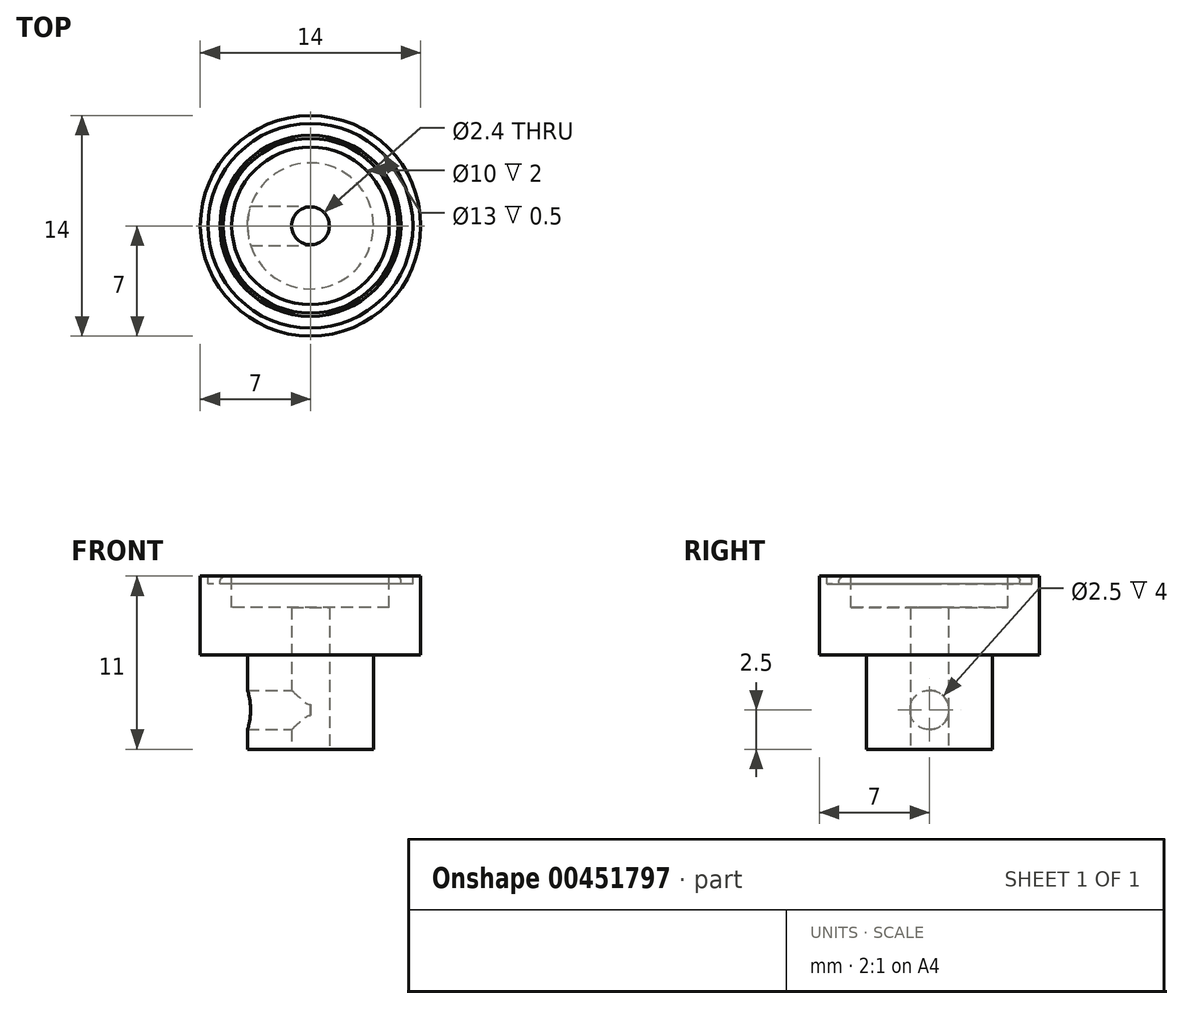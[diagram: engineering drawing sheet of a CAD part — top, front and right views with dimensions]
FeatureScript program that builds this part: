
annotation { "Feature Type Name" : "Feature", "Feature Type Description" : "" }
export const myFeature = defineFeature(function(context is Context, id is Id, definition is map)
    precondition{}
    {
        {
            var Q0;
            Q0=qCreatedBy(makeId("Top.planeOp"),FACE);
            var sketch = newSketch(context, id + "F0", { "sketchPlane" : qUnion([Q0])});
            skCircle(sketch, "E0", {"center": v(0, 0) * mm, "radius": 7 * mm});
            skSolve(sketch);
        }
        {
            var Q0;
            Q0 = qSketchRegion(id + "F0", true);
            extrude(context, id + "F1", {"entities" : qUnion([Q0]), "depth" : 5 * mm});
        }
        {
            var Q0;
            Q0=makeQuery(id+"F1.opExtrude","CAP_FACE",FACE,{"disambiguationData":[OSD([sQuery(id+"F0.wireOp",EDGE,"E0")])],"isStart":true});
            var sketch = newSketch(context, id + "F2", { "sketchPlane" : qUnion([Q0])});
            skCircle(sketch, "E1", {"center": v(0, 0) * mm, "radius": 4 * mm});
            skSolve(sketch);
        }
        {
            var Q0;
            Q0 = qSketchRegion(id + "F2", true);
            extrude(context, id + "F3", {"entities" : qUnion([Q0]), "operationType" : NewBodyOperationType.ADD, "depth" : 6 * mm});
        }
        {
            var Q0;
            Q0=makeQuery(id+"F3.opExtrude","CAP_FACE",FACE,{"disambiguationData":[OSD([sQuery(id+"F2.wireOp",EDGE,"E1")])],"isStart":false});
            var sketch = newSketch(context, id + "F4", { "sketchPlane" : qUnion([Q0])});
            skCircle(sketch, "E2", {"center": v(0, 0) * mm, "radius": 1.2 * mm});
            skSolve(sketch);
        }
        {
            var Q0;
            Q0 = qSketchRegion(id + "F4", true);
            extrude(context, id + "F5", {"entities" : qUnion([Q0]), "operationType" : NewBodyOperationType.REMOVE, "oppositeDirection" : true, "depth" : 9 * mm});
        }
        {
            var Q0;
            Q0=makeQuery(id+"F1.opExtrude","CAP_FACE",FACE,{"disambiguationData":[OSD([sQuery(id+"F0.wireOp",EDGE,"E0")])],"isStart":false});
            var sketch = newSketch(context, id + "F6", { "sketchPlane" : qUnion([Q0])});
            skCircle(sketch, "E3", {"center": v(0, 0) * mm, "radius": 5 * mm});
            skSolve(sketch);
        }
        {
            var Q0;
            Q0 = qSketchRegion(id + "F6", true);
            extrude(context, id + "F7", {"entities" : qUnion([Q0]), "operationType" : NewBodyOperationType.REMOVE, "oppositeDirection" : true, "depth" : 2 * mm});
        }
        {
            var Q0;
            Q0=makeQuery(id+"F1.opExtrude","CAP_FACE",FACE,{"disambiguationData":[OSD([sQuery(id+"F0.wireOp",EDGE,"E0")])],"isStart":false});
            var sketch = newSketch(context, id + "F8", { "sketchPlane" : qUnion([Q0])});
            skCircle(sketch, "E4", {"center": v(0, 0) * mm, "radius": 6.5 * mm});
            skCircle(sketch, "E5", {"center": v(0, 0) * mm, "radius": 5.75 * mm});
            skSolve(sketch);
        }
        {
            var Q0;
            Q0=makeQuery(id+"F8.imprint","IMPRINT",FACE,{"disambiguationData":[TD([[makeQuery(id+"F8.imprint","IMPRINT",EDGE,{"derivedFrom":sQuery(id+"F8.wireOp",EDGE,"E4")}),1.0]])]});
            extrude(context, id + "F9", {"entities" : qUnion([Q0]), "operationType" : NewBodyOperationType.REMOVE, "oppositeDirection" : true, "depth" : 0.5 * mm});
        }
        {
            var Q0;
            Q0=makeQuery(id+"F9.boolean.opBoolean","COPY",EDGE,{"derivedFrom":makeQuery(id+"F9.opExtrude","CAP_EDGE",EDGE,{"disambiguationData":[OSD([sQuery(id+"F8.wireOp",EDGE,"E5")])],"isStart":true})});
            chamfer(context, id + "F10", {"entities" : qUnion([Q0]), "width" : 0.2 * mm, "tangentPropagation" : true});
        }
        {
            var Q0;
            {var subQ0=sQuery(id+"F8.wireOp",EDGE,"E5");Q0=makeQuery(id+"F10.opChamfer","BLEND_EDGE",EDGE,{"blendedFrom":[makeQuery(id+"F9.boolean.opBoolean","COPY",EDGE,{"derivedFrom":makeQuery(id+"F9.opExtrude","CAP_EDGE",EDGE,{"disambiguationData":[OSD([subQ0])],"isStart":true})}),makeQuery(id+"F9.boolean.opBoolean","COPY",FACE,{"derivedFrom":makeQuery(id+"F9.opExtrude","SWEPT_FACE",FACE,{"disambiguationData":[OSD([subQ0])]})})],"blendedInto":[makeQuery(id+"F9.boolean.opBoolean","COPY",FACE,{"derivedFrom":makeQuery(id+"F9.opExtrude","SWEPT_FACE",FACE,{"disambiguationData":[OSD([subQ0])]})})]});}
            var Q1;
            Q1=makeQuery(id+"F5.boolean.opBoolean","COPY",EDGE,{"derivedFrom":makeQuery(id+"F5.opExtrude","CAP_EDGE",EDGE,{"disambiguationData":[OSD([sQuery(id+"F4.wireOp",EDGE,"E2")])],"isStart":false})});
            var Q2;
            Q2=makeQuery(id+"F5.boolean.opBoolean","COPY",EDGE,{"derivedFrom":makeQuery(id+"F5.opExtrude","CAP_EDGE",EDGE,{"disambiguationData":[OSD([sQuery(id+"F4.wireOp",EDGE,"E2")])],"isStart":true})});
            fillet(context, id + "F11", {"entities" : qUnion([Q0, Q1, Q2]), "radius" : 0.2 * mm, "tangentPropagation" : true, "allowEdgeOverflow" : false});
        }
        {
            var Q0;
            Q0=qCreatedBy(makeId("Top.planeOp"),FACE);
            cPlane(context, id + "F12", {"entities" : qUnion([Q0]), "cplaneType" : CPlaneType.OFFSET, "offset" : 5 * mm, "width" : 150 * mm, "height" : 150 * mm});
        }
        {
            var Q0;
            Q0=qCreatedBy(makeId("Right.planeOp"),FACE);
            var sketch = newSketch(context, id + "F13", { "sketchPlane" : qUnion([Q0])});
            skPoint(sketch, "E6", {"position": v(0, -3.5) * mm});
            skCircle(sketch, "E7", {"center": v(0, -3.5) * mm, "radius": 1.25 * mm});
            skSolve(sketch);
        }
        {
            var Q0;
            Q0 = qSketchRegion(id + "F13", true);
            extrude(context, id + "F14", {"entities" : qUnion([Q0]), "operationType" : NewBodyOperationType.REMOVE, "oppositeDirection" : true, "depth" : 4.5 * mm});
        }
    });
